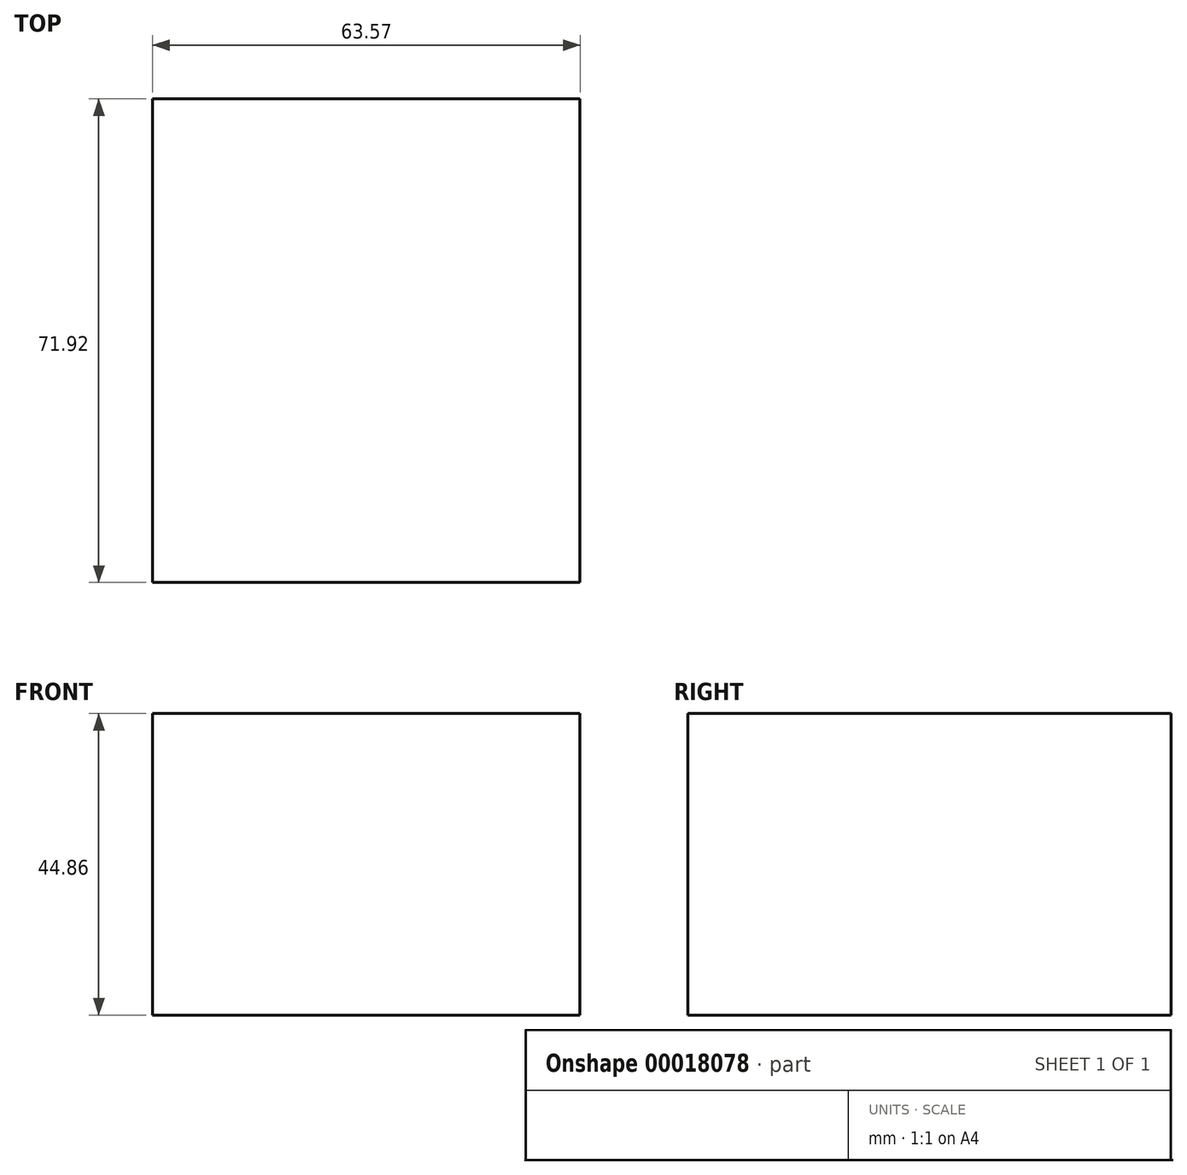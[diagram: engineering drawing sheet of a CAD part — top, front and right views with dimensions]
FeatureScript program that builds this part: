
annotation { "Feature Type Name" : "Feature", "Feature Type Description" : "" }
export const myFeature = defineFeature(function(context is Context, id is Id, definition is map)
    precondition{}
    {
        {
            var Q0;
            Q0=qCreatedBy(makeId("Front.planeOp"),FACE);
            var sketch = newSketch(context, id + "F0", { "sketchPlane" : qUnion([Q0])});
            skLineSegment(sketch, "E0.bottom", {"start": v(0, 0) * mm, "end": v(63.57, 0) * mm});
            skLineSegment(sketch, "E0.top", {"start": v(0, -44.86) * mm, "end": v(63.57, -44.86) * mm});
            skLineSegment(sketch, "E0.left", {"start": v(0, 0) * mm, "end": v(0, -44.86) * mm});
            skLineSegment(sketch, "E0.right", {"start": v(63.57, 0) * mm, "end": v(63.57, -44.86) * mm});
            skSolve(sketch);
        }
        {
            var Q0;
            Q0=makeQuery(id+"F0.imprint","IMPRINT",FACE,{"disambiguationData":[TD([[makeQuery(id+"F0.imprint","IMPRINT",EDGE,{"derivedFrom":sQuery(id+"F0.wireOp",EDGE,"E0.bottom")}),-1.0]])]});
            extrude(context, id + "F1", {"entities" : qUnion([Q0]), "depth" : 71.92 * mm});
        }
    });
